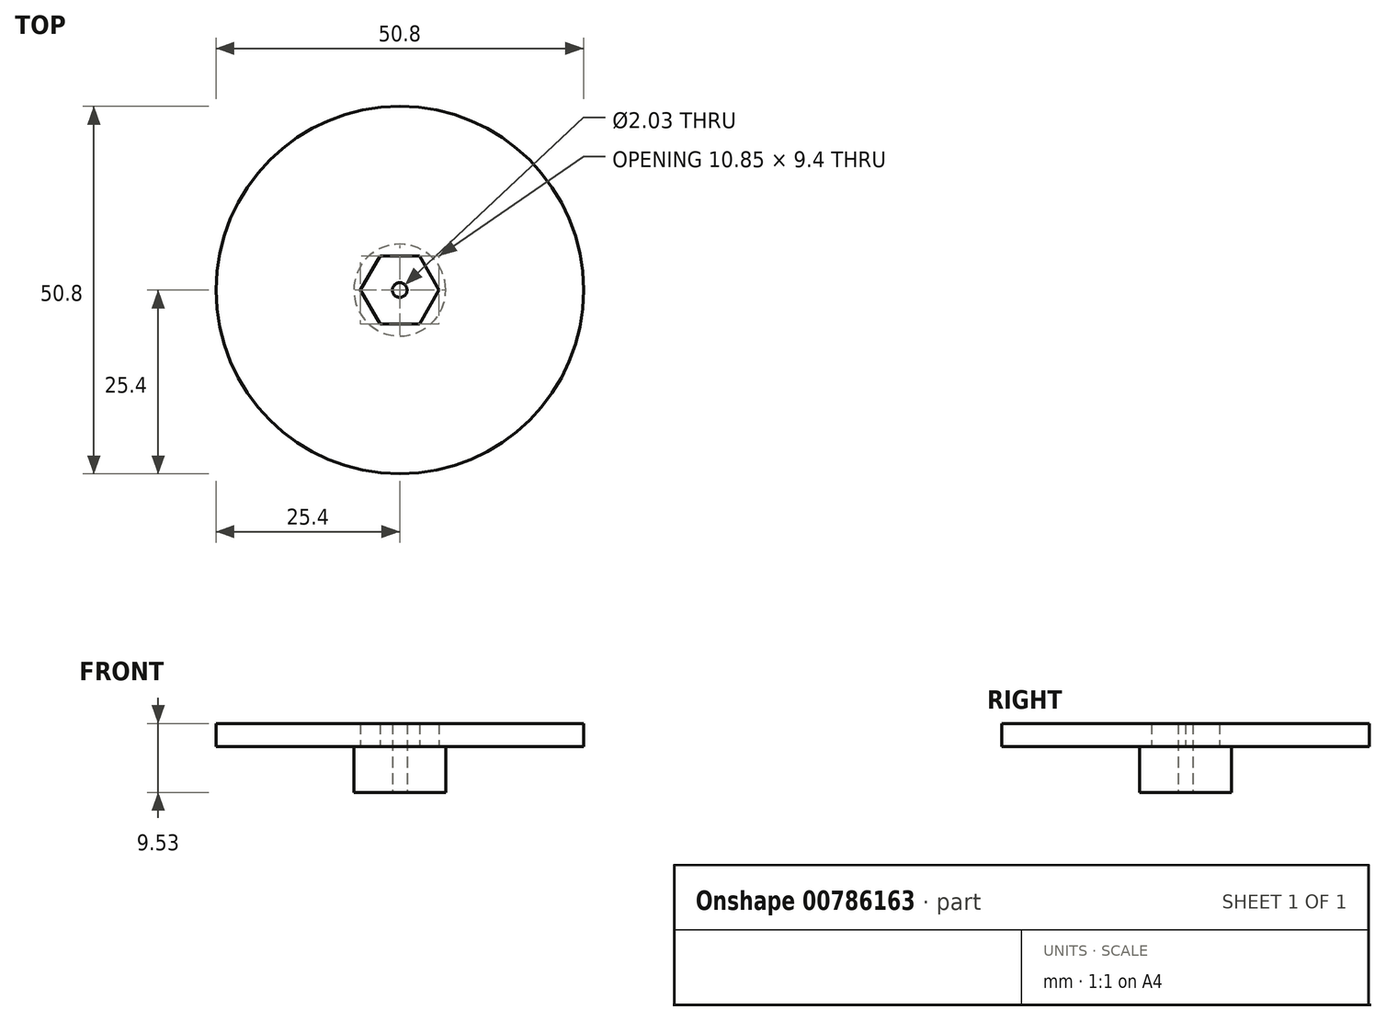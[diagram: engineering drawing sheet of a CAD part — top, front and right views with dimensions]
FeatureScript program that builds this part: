
annotation { "Feature Type Name" : "Feature", "Feature Type Description" : "" }
export const myFeature = defineFeature(function(context is Context, id is Id, definition is map)
    precondition{}
    {
        {
            var Q0;
            Q0=qCreatedBy(makeId("Top.planeOp"),FACE);
            var sketch = newSketch(context, id + "F0", { "sketchPlane" : qUnion([Q0])});
            skCircle(sketch, "E0", {"center": v(0, 0) * mm, "radius": 1.02 * mm});
            skCircle(sketch, "E1", {"center": v(0, 0) * mm, "radius": 6.35 * mm});
            skSolve(sketch);
        }
        {
            var Q0;
            Q0 = qSketchRegion(id + "F0", true);
            extrude(context, id + "F1", {"entities" : qUnion([Q0]), "depth" : 6.35 * mm, "offsetDistance" : 25.4 * mm});
        }
        {
            var Q0;
            Q0=makeQuery(id+"F1.opExtrude","CAP_FACE",FACE,{"disambiguationData":[OSD([sQuery(id+"F0.wireOp",EDGE,"E0"),sQuery(id+"F0.wireOp",EDGE,"E1")])],"isStart":false});
            var sketch = newSketch(context, id + "F2", { "sketchPlane" : qUnion([Q0])});
            skCircle(sketch, "E2.cCircle", {"center": v(0, 0) * mm, "radius": 4.7 * mm, "construction": true});
            skLineSegment(sketch, "E2.0", {"start": v(-2.71, 4.7) * mm, "end": v(2.71, 4.7) * mm});
            skLineSegment(sketch, "E2.1", {"start": v(2.71, 4.7) * mm, "end": v(5.43, 0) * mm});
            skLineSegment(sketch, "E2.2", {"start": v(5.43, 0) * mm, "end": v(2.71, -4.7) * mm});
            skLineSegment(sketch, "E2.3", {"start": v(2.71, -4.7) * mm, "end": v(-2.71, -4.7) * mm});
            skLineSegment(sketch, "E2.4", {"start": v(-2.71, -4.7) * mm, "end": v(-5.43, 0) * mm});
            skLineSegment(sketch, "E2.5", {"start": v(-5.43, 0) * mm, "end": v(-2.71, 4.7) * mm});
            skPoint(sketch, "E2.0.midPoint", {"position": v(0, 4.7) * mm});
            skSolve(sketch);
        }
        {
            var Q0;
            Q0=makeQuery(id+"F2.imprint","IMPRINT",FACE,{"disambiguationData":[TD([[makeQuery(id+"F2.imprint","IMPRINT",EDGE,{"derivedFrom":sQuery(id+"F2.wireOp",EDGE,"E2.0")}),-1.0]])]});
            var Q1;
            Q1=makeQuery(id+"F2.imprint","IMPRINT",FACE,{"disambiguationData":[TD([[makeQuery(id+"F2.imprint","IMPRINT",EDGE,{"derivedFrom":makeQuery(id+"F1.opExtrude","CAP_EDGE",EDGE,{"disambiguationData":[OSD([sQuery(id+"F0.wireOp",EDGE,"E0")])],"isStart":false})}),-1.0]])]});
            extrude(context, id + "F3", {"entities" : qUnion([Q0, Q1]), "operationType" : NewBodyOperationType.ADD, "depth" : 3.17 * mm, "offsetDistance" : 25.4 * mm});
        }
        {
            var Q0;
            Q0=makeQuery(id+"F1.opExtrude","CAP_FACE",FACE,{"disambiguationData":[OSD([sQuery(id+"F0.wireOp",EDGE,"E0"),sQuery(id+"F0.wireOp",EDGE,"E1")])],"isStart":false});
            var sketch = newSketch(context, id + "F4", { "sketchPlane" : qUnion([Q0])});
            skCircle(sketch, "E3", {"center": v(0, 0) * mm, "radius": 25.4 * mm});
            skSolve(sketch);
        }
        {
            var Q0;
            Q0=makeQuery(id+"F4.imprint","IMPRINT",FACE,{"disambiguationData":[TD([[makeQuery(id+"F4.imprint","IMPRINT",EDGE,{"derivedFrom":makeQuery(id+"F1.opExtrude","CAP_EDGE",EDGE,{"disambiguationData":[OSD([sQuery(id+"F0.wireOp",EDGE,"E1")])],"isStart":false})}),1.0]])]});
            var Q1;
            Q1=makeQuery(id+"F4.imprint","IMPRINT",FACE,{"disambiguationData":[TD([[makeQuery(id+"F4.imprint","IMPRINT",EDGE,{"derivedFrom":sQuery(id+"F4.wireOp",EDGE,"E3")}),1.0]])]});
            var Q2;
            Q2=makeQuery(id+"F3.opExtrude","CAP_FACE",FACE,{"disambiguationData":[OSD([sQuery(id+"F0.wireOp",EDGE,"E0"),sQuery(id+"F2.wireOp",EDGE,"E2.0"),sQuery(id+"F2.wireOp",EDGE,"E2.1"),sQuery(id+"F2.wireOp",EDGE,"E2.2"),sQuery(id+"F2.wireOp",EDGE,"E2.3"),sQuery(id+"F2.wireOp",EDGE,"E2.4"),sQuery(id+"F2.wireOp",EDGE,"E2.5")])],"isStart":false});
            extrude(context, id + "F5", {"entities" : qUnion([Q0, Q1]), "endBound" : BoundingType.UP_TO_SURFACE, "depth" : 25.4 * mm, "endBoundEntityFace" : qUnion([Q2]), "offsetDistance" : 25.4 * mm});
        }
    });
